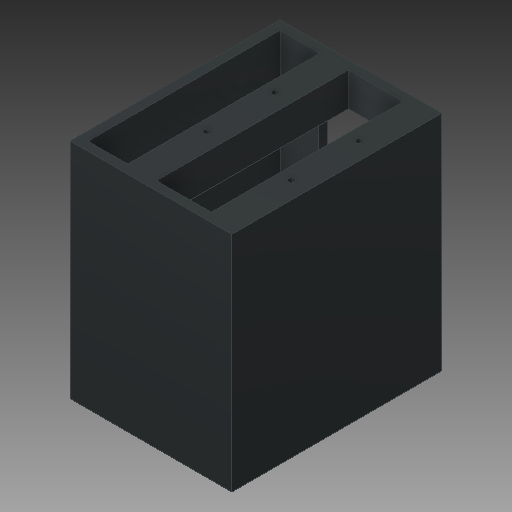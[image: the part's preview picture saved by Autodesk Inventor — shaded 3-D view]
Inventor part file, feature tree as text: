
AUTODESK INVENTOR PART (.ipt)
format: ipt  version: 2018 (Build 220112000, 112)  size: 174,080 bytes
history: native  units: mm
features: extrude x6, sketch x6
ambient origin geometry x8: Origin, YZ Plane, XZ Plane, XY Plane, X Axis, Y Axis, Z Axis, Center Point
bodies: Body1 (feature_tree)
feature tree (12):
  extrude  "Extrusion2"  Depth=548.0mm
  extrude  "Extrusion3"  Depth=583.0mm TaperAngle=0.0deg
  extrude  "Extrusion4"  Depth=345.0mm
  extrude  "Extrusion5"  Depth=88.0mm
  extrude  "Extrusion6"  Depth=75.0mm
  extrude  "Extrusion7"  Depth=583.0mm TaperAngle=0.0deg
  sketch  "Sketch1"  dims[d0=422.0mm d1=548.0mm]
  sketch  "Sketch2"  dims[d4=23.0mm d5=583.0mm d6=0.0mm]
  sketch  "Sketch3"  dims[d7=210.0mm d8=345.0mm]
  sketch  "Sketch4"  dims[d9=88.0mm d11=88.0mm]
  sketch  "Sketch5"  dims[d12=583.0mm d13=0.0mm d14=75.0mm]
  sketch  "Sketch6"  dims[d15=104.0mm d16=583.0mm d17=0.0mm d18=54.0mm d19=583.0mm d20=0.0mm d21=16.0mm d22=16.0mm d23=170.0mm d24=200.0mm d25=45.0mm d26=45.0mm d27=170.0mm d28=200.0mm d29=16.0mm d30=16.0mm d31=45.0mm d32=45.0mm d33=16.0mm d34=0.0mm d35=123.0mm d36=0.0mm]
